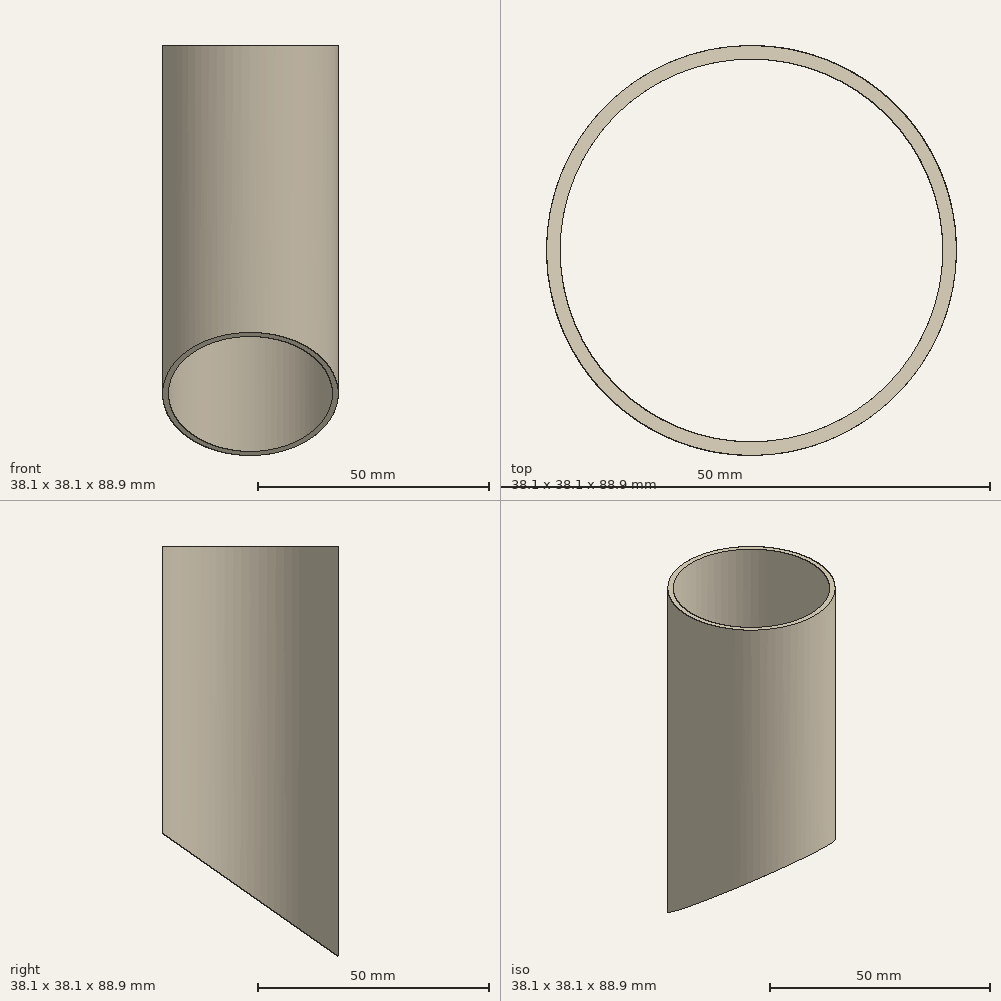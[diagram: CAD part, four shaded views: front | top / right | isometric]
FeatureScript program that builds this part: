
annotation { "Feature Type Name" : "Feature", "Feature Type Description" : "" }
export const myFeature = defineFeature(function(context is Context, id is Id, definition is map)
    precondition{}
    {
        {
            var Q0;
            Q0=qCreatedBy(makeId("Top.planeOp"),FACE);
            var sketch = newSketch(context, id + "F0", { "sketchPlane" : qUnion([Q0])});
            skCircle(sketch, "E0", {"center": v(0, 0) * mm, "radius": 19.05 * mm});
            skCircle(sketch, "E1", {"center": v(0, 0) * mm, "radius": 17.78 * mm});
            skSolve(sketch);
        }
        {
            var Q0;
            Q0 = qSketchRegion(id + "F0", true);
            extrude(context, id + "F1", {"entities" : qUnion([Q0]), "depth" : 88.9 * mm});
        }
        {
            var Q0;
            Q0=qCreatedBy(makeId("Right.planeOp"),FACE);
            var sketch = newSketch(context, id + "F2", { "sketchPlane" : qUnion([Q0])});
            skLineSegment(sketch, "E2", {"start": v(0, 0) * mm, "end": v(13.9, -9.73) * mm});
            skLineSegment(sketch, "E3", {"start": v(13.9, -9.73) * mm, "end": v(20.16, -0.78) * mm});
            skLineSegment(sketch, "E4", {"start": v(20.16, -0.78) * mm, "end": v(-52.38, 50.02) * mm});
            skLineSegment(sketch, "E5", {"start": v(-52.38, 50.02) * mm, "end": v(-58.65, 41.07) * mm});
            skLineSegment(sketch, "E6", {"start": v(-58.65, 41.07) * mm, "end": v(0, 0) * mm});
            skLineSegment(sketch, "E7.MirrorCS", {"start": v(13.9, -9.73) * mm, "end": v(7.63, -18.68) * mm});
            skLineSegment(sketch, "E8.MirrorCS", {"start": v(7.63, -18.68) * mm, "end": v(-64.92, 32.12) * mm});
            skLineSegment(sketch, "E9.MirrorCS", {"start": v(-64.92, 32.12) * mm, "end": v(-58.65, 41.07) * mm});
            skSolve(sketch);
        }
        {
            var Q0;
            Q0 = qSketchRegion(id + "F2", true);
            extrude(context, id + "F3", {"entities" : qUnion([Q0]), "operationType" : NewBodyOperationType.REMOVE, "endBound" : BoundingType.SYMMETRIC, "oppositeDirection" : true, "depth" : 38.1 * mm});
        }
    });
